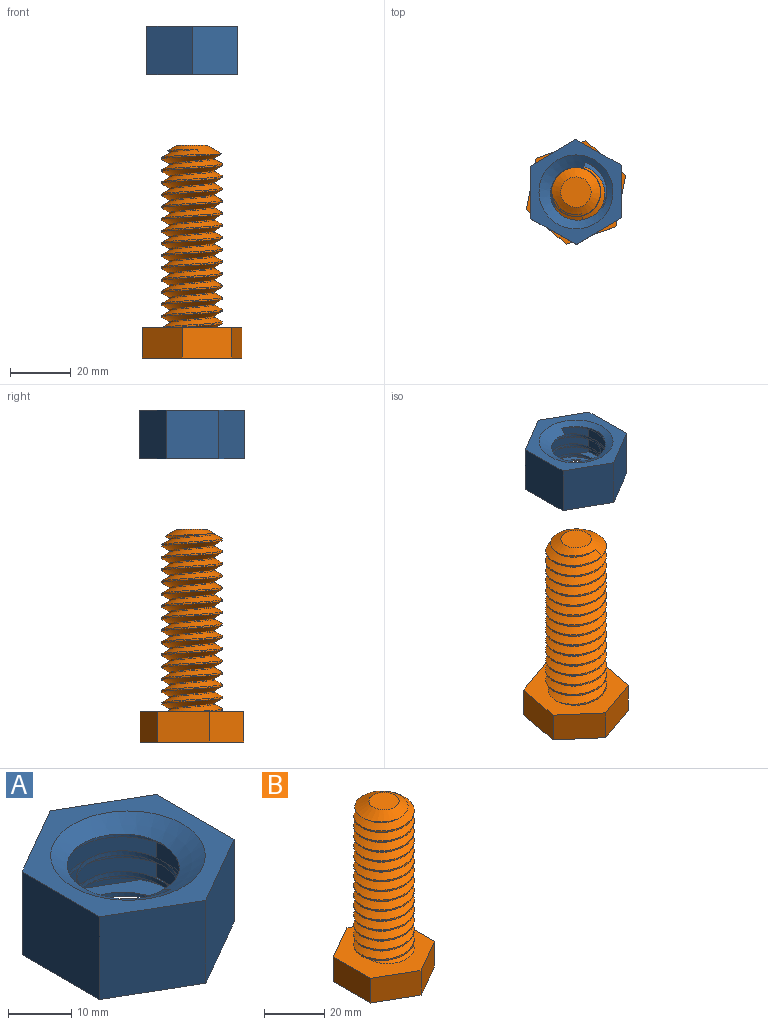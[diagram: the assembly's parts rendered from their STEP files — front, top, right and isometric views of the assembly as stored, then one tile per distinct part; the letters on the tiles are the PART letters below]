
ASSEMBLY  parts=2 mates=1
PART A: 12 faces, bbox 30x34.6x16 mm
  f0: plane 34.64x30mm, normal (0,0,1), area 311.8mm2, adj f2,f3,f4,f5,f6,f7,f9
  f1: plane 34.64x30mm, normal (0,0,-1), area 311.8mm2, adj f2,f3,f4,f5,f6,f7,f8
  f2: plane 17.32x16mm, normal (-1,0,0), area 277.1mm2, adj f0,f1,f3,f7
  f3: plane 16x15mm, normal (-0.5,-0.87,0), area 277.1mm2, adj f0,f1,f2,f4
  f4: plane 16x15mm, normal (0.5,-0.87,0), area 277.1mm2, adj f0,f1,f3,f5
  f5: plane 17.32x16mm, normal (1,0,0), area 277.1mm2, adj f0,f1,f4,f6
  f6: plane 16x15mm, normal (0.5,0.87,0), area 277.1mm2, adj f0,f1,f5,f7
  f7: plane 16x15mm, normal (-0.5,0.87,0), area 277.1mm2, adj f0,f1,f2,f6
  f8: cone r=12.2mm half-angle=60deg, axis (0,0,-1), area 235.6mm2, adj f1,f10,f11
  f9: cone r=8.1mm half-angle=60deg, axis (0,0,1), area 235.7mm2, adj f0,f10,f11
  f10: cylinder r=8.1mm len=16.2mm, axis (0,0,-1), area 122mm2, adj f8,f9
  f11: cylinder r=10.2mm len=20.4mm, axis (0,0,-1), area 151.1mm2, adj f8,f9
PART B: 14 faces, bbox 31.6x36.2x72.3 mm
  f0: plane 17.32x10mm, normal (-1,0,0), area 173.2mm2, adj f1,f5,f6,f7
  f1: plane 15x10mm, normal (-0.5,-0.87,0), area 173.2mm2, adj f0,f2,f6,f7
  f2: plane 15x10mm, normal (0.5,-0.87,0), area 173.2mm2, adj f1,f3,f6,f7
  f3: plane 17.32x10mm, normal (1,0,0), area 173.2mm2, adj f2,f4,f6,f7
  f4: plane 15x10mm, normal (0.5,0.87,0), area 173.2mm2, adj f3,f5,f6,f7
  f5: plane 15x10mm, normal (-0.5,0.87,0), area 173.2mm2, adj f0,f4,f6,f7
  f6: plane 36.22x31.58mm, normal (0,0,1), area 538.9mm2, adj f0,f1,f2,f3,f4,f5,f8,f11
  f7: plane 34.64x30mm, normal (0,0,-1), area 779.4mm2, adj f0,f1,f2,f3,f4,f5
  f8: cylinder r=10mm len=57.11mm, axis (0,0,-1), area 504.4mm2, adj f6,f10,f11,f13
  f9: plane 10x10mm, normal (0,0,1), area 78.5mm2, adj f10
  f10: cone r=5mm half-angle=60deg, axis (0,0,-1), area 187.2mm2, adj f8,f9,f11,f12,f13
  f11: bspline ~60.83x23.09mm, area 2386.8mm2, adj f6,f8,f10,f12
  f12: cylinder r=7.4mm len=58.61mm, axis (0,0,1), area 493.9mm2, adj f6,f10,f11,f13
  f13: bspline ~62.17x23.09mm, area 2374.9mm2, adj f6,f8,f10,f12
PLACE A rot(axis=(-0.49,-0.87,0),180deg) t=(76.15,-22.33,125.12)mm
PLACE B rot(axis=(0,0,-1),130.8deg) t=(76.15,-22.33,-6.23)mm fixed
MATE cylindrical B.f8 <-> A.f8  axis (0,0,-1) through (76.15,-22.33,32.32)mm
